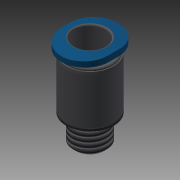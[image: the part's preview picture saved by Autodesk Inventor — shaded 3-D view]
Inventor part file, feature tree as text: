
AUTODESK INVENTOR PART (.ipt)
format: ipt  version: 2018 (Build 220112000, 112)  size: 214,016 bytes
history: native  units: mm
features: other x28, sketch x4, revolve x2, extrude x2, thread x1
ambient origin geometry x8: Origin, YZ Plane, XZ Plane, XY Plane, X Axis, Y Axis, Z Axis, Center Point
bodies: Solid1 (feature_tree)
feature tree (37):
  revolve  "Revolution1"  [1 undecoded]
  thread  "Thread1"  [1 undecoded]
  extrude  "Extrusion1"  TaperAngle=360.0deg  [1 undecoded]
  extrude  "Extrusion2"  TaperAngle=0.0deg  [1 undecoded]
  revolve  "Revolution2"  [1 undecoded]
  other  "ANBAU_XY"
  other  "ANBAU_YZ"
  other  "ANBAU_ZX"
  other  "ANBAU_X"
  other  "ANBAU_Y"
  other  "ANBAU_Z"
  other  "ANBAU_Center"
  other  "ANBAU_STD_XY"
  other  "ANBAU_STD_YZ"
  other  "ANBAU_STD_ZX"
  other  "ANBAU_STD_X"
  other  "ANBAU_STD_Y"
  other  "ANBAU_STD_Z"
  other  "ANBAU_STD_Center"
  other  "CPV_XY"
  other  "CPV_YZ"
  other  "CPV_ZX"
  other  "CPV_X"
  other  "CPV_Y"
  other  "CPV_Z"
  other  "CPV_Center"
  other  "CPV_ANBAU_XY"
  other  "CPV_ANBAU_YZ"
  other  "CPV_ANBAU_ZX"
  other  "CPV_ANBAU_X"
  other  "CPV_ANBAU_Y"
  other  "CPV_ANBAU_Z"
  other  "CPV_ANBAU_Center"
  sketch  "Sketch_1"  dims[d0=360.0deg d1=4.3865mm d2=0.0mm d3=1.5mm d4=0.0mm]
  sketch  "Sketch_2"  dims[d5=7.2mm d6=0.0mm d7=360.0deg]
  sketch  "Sketch_3"  dims[d8=0.0mm d9=0.0mm]
  sketch  "Sketch_4"  dims[d10=0.0mm d11=0.0mm]
note: 5 required parameter values undecoded (feature->parameter linkage not recoverable at this tier; creation-order binding heuristic only, values carry confidence <= 0.55)